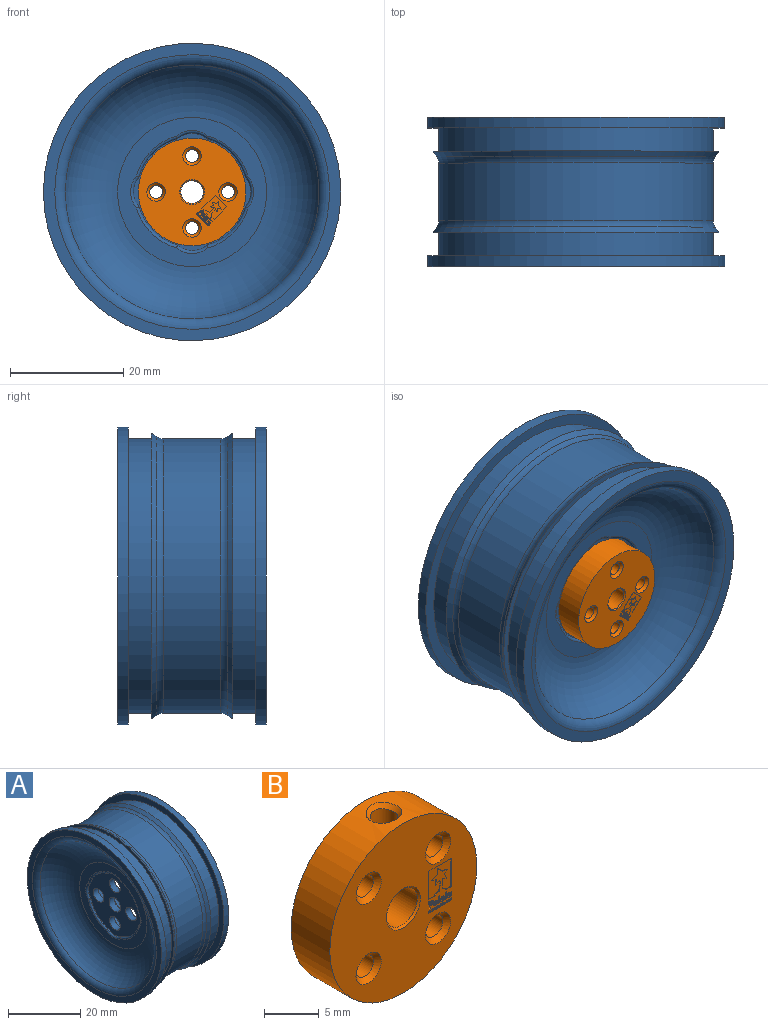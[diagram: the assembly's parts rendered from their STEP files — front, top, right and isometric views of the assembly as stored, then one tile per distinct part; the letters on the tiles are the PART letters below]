
ASSEMBLY  parts=2 mates=1
PART A: 63 faces, bbox 30.2x55.6x55.6 mm
  f0: cylinder r=9.75mm len=6.81mm, axis (-1,0,0), area 1mm2, adj f33,f45,f46,f54
  f1: cylinder r=9.75mm len=6.81mm, axis (-1,0,0), area 1mm2, adj f33,f43,f46,f50
  f2: cylinder r=9.75mm len=6.81mm, axis (-1,0,0), area 1mm2, adj f33,f44,f45,f51
  f3: cylinder r=9.75mm len=6.81mm, axis (-1,0,0), area 1mm2, adj f33,f43,f44,f47
  f4: cylinder r=9.75mm len=6.81mm, axis (1,0,0), area 1mm2, adj f34,f41,f42,f58
  f5: cylinder r=9.75mm len=6.81mm, axis (1,0,0), area 1mm2, adj f34,f40,f42,f62
  f6: cylinder r=9.75mm len=6.81mm, axis (1,0,0), area 1mm2, adj f34,f39,f41,f55
  f7: cylinder r=9.75mm len=6.81mm, axis (1,0,0), area 1mm2, adj f34,f39,f40,f59
  f8: cylinder r=2.25mm len=4.5mm, axis (-1,0,0), area 28.3mm2, adj f33,f34
  f9: plane 52.5x52.5mm, normal (1,0,0), area 317.3mm2, adj f10,f30
  f10: cylinder r=26.25mm len=52.5mm, axis (1,0,0), area 305.1mm2, adj f9,f11
  f11: plane 52.5x52.5mm, normal (-1,0,0), area 317.3mm2, adj f10,f12
  f12: torus R=24.25mm, axis (1,0,0), area 343.3mm2, adj f11,f13
  f13: torus R=13.17mm, axis (1,0,0), area 1361.5mm2, adj f12,f14
  f14: plane 26.33x26.33mm, normal (-1,0,0), area 205.2mm2, adj f13,f47,f48,f49,f50,f51,f52,f53
  f15: cylinder r=12.95mm len=25.89mm, axis (1,0,0), area 3.3mm2, adj f16,f31
  f16: torus R=12.25mm, axis (1,0,0), area 1782.1mm2, adj f15,f17
  f17: cylinder r=22.25mm len=44.5mm, axis (1,0,0), area 529.5mm2, adj f16,f18
  f18: torus R=24.25mm, axis (1,0,0), area 453.5mm2, adj f17,f19
  f19: plane 52.5x52.5mm, normal (1,0,0), area 317.3mm2, adj f18,f20
  f20: cylinder r=26.25mm len=52.5mm, axis (1,0,0), area 305.1mm2, adj f19,f21
  f21: plane 52.5x52.5mm, normal (-1,0,0), area 317.3mm2, adj f20,f22
  f22: cylinder r=24.25mm len=48.5mm, axis (1,0,0), area 624.7mm2, adj f21,f23
  f23: plane 50.5x50.5mm, normal (1,0,0), area 155.5mm2, adj f22,f24
  f24: cone r=25.25mm half-angle=33.7deg, axis (1,0,0), area 187.4mm2, adj f23,f25
  f25: torus R=26.25mm, axis (1,0,0), area 180mm2, adj f24,f26
  f26: cylinder r=24.25mm len=48.5mm, axis (1,0,0), area 1552.5mm2, adj f25,f27
  f27: torus R=26.25mm, axis (1,0,0), area 180mm2, adj f26,f28
  f28: cone r=24.59mm half-angle=33.7deg, axis (-1,0,0), area 187.4mm2, adj f27,f29
  f29: plane 50.5x50.5mm, normal (-1,0,0), area 155.5mm2, adj f28,f30
  f30: cylinder r=24.25mm len=48.5mm, axis (1,0,0), area 624.7mm2, adj f9,f29
  f31: cylinder r=12.95mm len=25.89mm, axis (-1,0,0), area 1.9mm2, adj f15,f32
  f32: plane 25.89x25.89mm, normal (1,0,0), area 187mm2, adj f31,f55,f56,f57,f58,f59,f60,f61
  f33: plane 20.7x20.7mm, normal (-1,0,0), area 235.9mm2, adj f0,f1,f2,f3,f8,f35,f36,f37
  f34: plane 20.7x20.7mm, normal (1,0,0), area 235.9mm2, adj f4,f5,f6,f7,f8,f35,f36,f37
  f35: cylinder r=2.1mm len=4.2mm, axis (1,0,0), area 26.4mm2, adj f33,f34
  f36: cylinder r=2.1mm len=4.2mm, axis (1,0,0), area 26.4mm2, adj f33,f34
  f37: cylinder r=2.1mm len=4.2mm, axis (1,0,0), area 26.4mm2, adj f33,f34
  f38: cylinder r=2.1mm len=4.2mm, axis (1,0,0), area 26.4mm2, adj f33,f34
  f39: cylinder r=4mm len=5.18mm, axis (-1,0,0), area 0.6mm2, adj f6,f7,f34,f57
  f40: cylinder r=4mm len=5.18mm, axis (-1,0,0), area 0.6mm2, adj f5,f7,f34,f61
  f41: cylinder r=4mm len=5.18mm, axis (-1,0,0), area 0.6mm2, adj f4,f6,f34,f56
  f42: cylinder r=4mm len=5.18mm, axis (-1,0,0), area 0.6mm2, adj f4,f5,f34,f60
  f43: cylinder r=4mm len=5.18mm, axis (1,0,0), area 0.6mm2, adj f1,f3,f33,f48
  f44: cylinder r=4mm len=5.18mm, axis (1,0,0), area 0.6mm2, adj f2,f3,f33,f49
  f45: cylinder r=4mm len=5.18mm, axis (1,0,0), area 0.6mm2, adj f0,f2,f33,f53
  f46: cylinder r=4mm len=5.18mm, axis (1,0,0), area 0.6mm2, adj f0,f1,f33,f52
  f47: torus R=10.25mm, axis (-1,0,0), area 8mm2, adj f3,f14,f48,f49
  f48: torus R=4.5mm, axis (-1,0,0), area 4.5mm2, adj f14,f43,f47,f50
  f49: torus R=4.5mm, axis (-1,0,0), area 4.5mm2, adj f14,f44,f47,f51
  f50: torus R=10.25mm, axis (-1,0,0), area 8mm2, adj f1,f14,f48,f52
  f51: torus R=10.25mm, axis (-1,0,0), area 8mm2, adj f2,f14,f49,f53
  f52: torus R=4.5mm, axis (-1,0,0), area 4.5mm2, adj f14,f46,f50,f54
  f53: torus R=4.5mm, axis (-1,0,0), area 4.5mm2, adj f14,f45,f51,f54
  f54: torus R=10.25mm, axis (-1,0,0), area 8mm2, adj f0,f14,f52,f53
  f55: torus R=10.25mm, axis (-1,0,0), area 8mm2, adj f6,f32,f56,f57
  f56: torus R=4.5mm, axis (-1,0,0), area 4.5mm2, adj f32,f41,f55,f58
  f57: torus R=4.5mm, axis (-1,0,0), area 4.5mm2, adj f32,f39,f55,f59
  f58: torus R=10.25mm, axis (-1,0,0), area 8mm2, adj f4,f32,f56,f60
  f59: torus R=10.25mm, axis (-1,0,0), area 8mm2, adj f7,f32,f57,f61
  f60: torus R=4.5mm, axis (-1,0,0), area 4.5mm2, adj f32,f42,f58,f62
  f61: torus R=4.5mm, axis (-1,0,0), area 4.5mm2, adj f32,f40,f59,f62
  f62: torus R=10.25mm, axis (-1,0,0), area 8mm2, adj f5,f32,f60,f61
PART B: 267 faces, bbox 19x5x19 mm
  f0: bspline ~3.36x3.21mm, area 5.4mm2, adj f11,f17
  f1: cone r=2mm half-angle=45deg, axis (0,-1,0), area 3.7mm2, adj f12,f18
  f2: cone r=2mm half-angle=45deg, axis (0,1,0), area 3.7mm2, adj f12,f19
  f3: cone r=1.13mm half-angle=45deg, axis (0,1,0), area 6.1mm2, adj f14,f19
  f4: cone r=1.13mm half-angle=45deg, axis (0,1,0), area 6.1mm2, adj f15,f19
  f5: cone r=1.13mm half-angle=45deg, axis (0,1,0), area 6.1mm2, adj f16,f19
  f6: cone r=1.13mm half-angle=45deg, axis (0,1,0), area 6.1mm2, adj f13,f19
  f7: cone r=1.63mm half-angle=45deg, axis (0,-1,0), area 6.1mm2, adj f13,f18
  f8: cone r=1.63mm half-angle=45deg, axis (0,-1,0), area 6.1mm2, adj f14,f18
  f9: cone r=1.63mm half-angle=45deg, axis (0,-1,0), area 6.1mm2, adj f16,f18
  f10: cone r=1.63mm half-angle=45deg, axis (0,-1,0), area 6.1mm2, adj f15,f18
  f11: cylinder r=1.25mm len=7.5mm, axis (0,0,1), area 56.6mm2, adj f0,f12
  f12: cylinder r=2mm len=4.6mm, axis (0,1,0), area 54.4mm2, adj f1,f2,f11
  f13: cylinder r=1.13mm len=4mm, axis (0,1,0), area 28.4mm2, adj f6,f7
  f14: cylinder r=1.13mm len=4mm, axis (0,1,0), area 28.4mm2, adj f3,f8
  f15: cylinder r=1.13mm len=4mm, axis (0,1,0), area 28.4mm2, adj f4,f10
  f16: cylinder r=1.13mm len=4mm, axis (0,1,0), area 28.4mm2, adj f5,f9
  f17: cylinder r=9.5mm len=19mm, axis (0,-1,0), area 289.9mm2, adj f0,f18,f19
  f18: plane 19x19mm, normal (0,-1,0), area 226.4mm2, adj f1,f7,f8,f9,f10,f17,f20,f21
  f19: plane 19x19mm, normal (0,1,0), area 234.9mm2, adj f2,f3,f4,f5,f6,f17
  f20: plane 0.05x0.04mm, normal (0,0,-1), area 0mm2, adj f18,f21,f32,f33
  f21: plane 0.2x0.05mm, normal (-0.97,0,0.25), area 0mm2, adj f18,f20,f22,f33
  f22: plane 0.05x0.03mm, normal (0,0,1), area 0mm2, adj f18,f21,f23,f33
  f23: plane 0.16x0.05mm, normal (0.95,0,0.31), area 0mm2, adj f18,f22,f24,f33
  f24: plane 0.16x0.05mm, normal (-0.95,0,0.31), area 0mm2, adj f18,f23,f25,f33
  f25: plane 0.05x0.03mm, normal (0,0,1), area 0mm2, adj f18,f24,f26,f33
  f26: plane 0.2x0.05mm, normal (0.97,0,0.25), area 0mm2, adj f18,f25,f27,f33
  f27: plane 0.05x0.04mm, normal (0,0,-1), area 0mm2, adj f18,f26,f28,f33
  f28: plane 0.16x0.05mm, normal (-0.97,0,-0.23), area 0mm2, adj f18,f27,f29,f33
  f29: plane 0.16x0.05mm, normal (0.95,0,-0.31), area 0mm2, adj f18,f28,f30,f33
  f30: plane 0.05x0.03mm, normal (0,0,-1), area 0mm2, adj f18,f29,f31,f33
  f31: plane 0.16x0.05mm, normal (-0.95,0,-0.31), area 0mm2, adj f18,f30,f32,f33
  f32: plane 0.16x0.05mm, normal (0.98,0,-0.21), area 0mm2, adj f18,f20,f31,f33
  f33: plane 0.27x0.2mm, normal (0,-1,0), area 0mm2, adj f20,f21,f22,f23,f24,f25,f26,f27
  f34: plane 0.05x0.04mm, normal (0,0,-1), area 0mm2, adj f18,f35,f46,f47
  f35: plane 0.2x0.05mm, normal (-0.97,0,0.25), area 0mm2, adj f18,f34,f36,f47
  f36: plane 0.05x0.03mm, normal (0,0,1), area 0mm2, adj f18,f35,f37,f47
  f37: plane 0.16x0.05mm, normal (0.95,0,0.31), area 0mm2, adj f18,f36,f38,f47
  f38: plane 0.16x0.05mm, normal (-0.95,0,0.31), area 0mm2, adj f18,f37,f39,f47
  f39: plane 0.05x0.03mm, normal (0,0,1), area 0mm2, adj f18,f38,f40,f47
  f40: plane 0.2x0.05mm, normal (0.97,0,0.25), area 0mm2, adj f18,f39,f41,f47
  f41: plane 0.05x0.04mm, normal (0,0,-1), area 0mm2, adj f18,f40,f42,f47
  f42: plane 0.16x0.05mm, normal (-0.97,0,-0.23), area 0mm2, adj f18,f41,f43,f47
  f43: plane 0.16x0.05mm, normal (0.95,0,-0.31), area 0mm2, adj f18,f42,f44,f47
  f44: plane 0.05x0.03mm, normal (0,0,-1), area 0mm2, adj f18,f43,f45,f47
  f45: plane 0.16x0.05mm, normal (-0.95,0,-0.31), area 0mm2, adj f18,f44,f46,f47
  f46: plane 0.16x0.05mm, normal (0.98,0,-0.21), area 0mm2, adj f18,f34,f45,f47
  f47: plane 0.27x0.2mm, normal (0,-1,0), area 0mm2, adj f34,f35,f36,f37,f38,f39,f40,f41
  f48: plane 0.05x0.04mm, normal (0,0,-1), area 0mm2, adj f18,f49,f60,f61
  f49: plane 0.2x0.05mm, normal (-0.97,0,0.25), area 0mm2, adj f18,f48,f50,f61
  f50: plane 0.05x0.03mm, normal (0,0,1), area 0mm2, adj f18,f49,f51,f61
  f51: plane 0.16x0.05mm, normal (0.95,0,0.31), area 0mm2, adj f18,f50,f52,f61
  f52: plane 0.16x0.05mm, normal (-0.95,0,0.31), area 0mm2, adj f18,f51,f53,f61
  f53: plane 0.05x0.03mm, normal (0,0,1), area 0mm2, adj f18,f52,f54,f61
  f54: plane 0.2x0.05mm, normal (0.97,0,0.25), area 0mm2, adj f18,f53,f55,f61
  f55: plane 0.05x0.04mm, normal (0,0,-1), area 0mm2, adj f18,f54,f56,f61
  f56: plane 0.16x0.05mm, normal (-0.97,0,-0.23), area 0mm2, adj f18,f55,f57,f61
  f57: plane 0.16x0.05mm, normal (0.95,0,-0.31), area 0mm2, adj f18,f56,f58,f61
  f58: plane 0.05x0.03mm, normal (0,0,-1), area 0mm2, adj f18,f57,f59,f61
  f59: plane 0.16x0.05mm, normal (-0.95,0,-0.31), area 0mm2, adj f18,f58,f60,f61
  f60: plane 0.16x0.05mm, normal (0.98,0,-0.21), area 0mm2, adj f18,f48,f59,f61
  f61: plane 0.27x0.2mm, normal (0,-1,0), area 0mm2, adj f48,f49,f50,f51,f52,f53,f54,f55
  f62: plane 0.05x0.05mm, normal (-1,0,0), area 0mm2, adj f18,f63,f65,f66
  f63: plane 0.05x0.04mm, normal (0,0,1), area 0mm2, adj f18,f62,f64,f66
  f64: plane 0.05x0.05mm, normal (1,0,0), area 0mm2, adj f18,f63,f65,f66
  f65: plane 0.05x0.04mm, normal (0,0,-1), area 0mm2, adj f18,f62,f64,f66
  f66: plane 0.05x0.04mm, normal (0,-1,0), area 0mm2, adj f62,f63,f64,f65
  f67: bspline ~0.1x0.08mm, area 0mm2, adj f18,f68,f76,f77
  f68: bspline ~0.08x0.05mm, area 0mm2, adj f18,f67,f69,f77
  f69: bspline ~0.06x0.05mm, area 0mm2, adj f18,f68,f70,f77
  f70: bspline ~0.05x0.05mm, area 0mm2, adj f18,f69,f71,f77
  f71: plane 0.09x0.05mm, normal (-1,0,0), area 0mm2, adj f18,f70,f72,f77
  f72: plane 0.05x0.03mm, normal (0,0,1), area 0mm2, adj f18,f71,f73,f77
  f73: plane 0.28x0.05mm, normal (1,0,0), area 0mm2, adj f18,f72,f74,f77
  f74: plane 0.05x0.03mm, normal (0,0,-1), area 0mm2, adj f18,f73,f75,f77
  f75: plane 0.05x0.02mm, normal (-1,0,0), area 0mm2, adj f18,f74,f76,f77
  f76: bspline ~0.07x0.05mm, area 0mm2, adj f18,f67,f75,f77
  f77: plane 0.28x0.17mm, normal (0,-1,0), area 0mm2, adj f67,f68,f69,f70,f71,f72,f73,f74
  f78: bspline ~0.08x0.06mm, area 0mm2, adj f77,f79,f82,f83
  f79: bspline ~0.05x0.05mm, area 0mm2, adj f77,f78,f80,f83
  f80: plane 0.12x0.05mm, normal (-1,0,0), area 0mm2, adj f77,f79,f81,f83
  f81: bspline ~0.06x0.05mm, area 0mm2, adj f77,f80,f82,f83
  f82: bspline ~0.07x0.05mm, area 0mm2, adj f77,f78,f81,f83
  f83: plane 0.15x0.11mm, normal (0,-1,0), area 0mm2, adj f78,f79,f80,f81,f82
  f84: bspline ~0.11x0.09mm, area 0mm2, adj f18,f85,f87,f88
  f85: bspline ~0.11x0.09mm, area 0mm2, adj f18,f84,f86,f88
  f86: bspline ~0.11x0.09mm, area 0mm2, adj f18,f85,f87,f88
  f87: bspline ~0.11x0.09mm, area 0mm2, adj f18,f84,f86,f88
  f88: plane 0.22x0.18mm, normal (0,-1,0), area 0mm2, adj f84,f85,f86,f87,f89,f90,f91,f92
  f89: bspline ~0.08x0.06mm, area 0mm2, adj f88,f90,f92,f93
  f90: bspline ~0.08x0.06mm, area 0mm2, adj f88,f89,f91,f93
  f91: bspline ~0.08x0.06mm, area 0mm2, adj f88,f90,f92,f93
  f92: bspline ~0.08x0.06mm, area 0mm2, adj f88,f89,f91,f93
  f93: plane 0.15x0.12mm, normal (0,-1,0), area 0mm2, adj f89,f90,f91,f92
  f94: plane 0.28x0.05mm, normal (-1,0,0), area 0mm2, adj f18,f95,f97,f98
  f95: plane 0.05x0.03mm, normal (0,0,1), area 0mm2, adj f18,f94,f96,f98
  f96: plane 0.28x0.05mm, normal (1,0,0), area 0mm2, adj f18,f95,f97,f98
  f97: plane 0.05x0.03mm, normal (0,0,-1), area 0mm2, adj f18,f94,f96,f98
  f98: plane 0.28x0.03mm, normal (0,-1,0), area 0mm2, adj f94,f95,f96,f97
  f99: bspline ~0.11x0.09mm, area 0mm2, adj f18,f100,f102,f103
  f100: bspline ~0.11x0.09mm, area 0mm2, adj f18,f99,f101,f103
  f101: bspline ~0.11x0.09mm, area 0mm2, adj f18,f100,f102,f103
  f102: bspline ~0.11x0.09mm, area 0mm2, adj f18,f99,f101,f103
  f103: plane 0.22x0.18mm, normal (0,-1,0), area 0mm2, adj f99,f100,f101,f102,f104,f105,f106,f107
  f104: bspline ~0.08x0.06mm, area 0mm2, adj f103,f105,f107,f108
  f105: bspline ~0.08x0.06mm, area 0mm2, adj f103,f104,f106,f108
  f106: bspline ~0.08x0.06mm, area 0mm2, adj f103,f105,f107,f108
  f107: bspline ~0.08x0.06mm, area 0mm2, adj f103,f104,f106,f108
  f108: plane 0.15x0.12mm, normal (0,-1,0), area 0mm2, adj f104,f105,f106,f107
  f109: plane 0.28x0.05mm, normal (-1,0,0), area 0mm2, adj f18,f110,f112,f113
  f110: plane 0.05x0.03mm, normal (0,0,1), area 0mm2, adj f18,f109,f111,f113
  f111: plane 0.28x0.05mm, normal (1,0,0), area 0mm2, adj f18,f110,f112,f113
  f112: plane 0.05x0.03mm, normal (0,0,-1), area 0mm2, adj f18,f109,f111,f113
  f113: plane 0.28x0.03mm, normal (0,-1,0), area 0mm2, adj f109,f110,f111,f112
  f114: plane 0.2x0.05mm, normal (-1,0,0), area 0mm2, adj f18,f115,f126,f127
  f115: plane 0.05x0.03mm, normal (0,0,1), area 0mm2, adj f18,f114,f116,f127
  f116: plane 0.05x0.02mm, normal (1,0,0), area 0mm2, adj f18,f115,f117,f127
  f117: bspline ~0.07x0.05mm, area 0mm2, adj f18,f116,f118,f127
  f118: bspline ~0.08x0.07mm, area 0mm2, adj f18,f117,f119,f127
  f119: plane 0.13x0.05mm, normal (1,0,0), area 0mm2, adj f18,f118,f120,f127
  f120: plane 0.05x0.03mm, normal (0,0,-1), area 0mm2, adj f18,f119,f121,f127
  f121: plane 0.12x0.05mm, normal (-1,0,0), area 0mm2, adj f18,f120,f122,f127
  f122: bspline ~0.05x0.05mm, area 0mm2, adj f18,f121,f123,f127
  f123: bspline ~0.05x0.03mm, area 0mm2, adj f18,f122,f124,f127
  f124: bspline ~0.06x0.05mm, area 0mm2, adj f18,f123,f125,f127
  f125: plane 0.15x0.05mm, normal (1,0,0), area 0mm2, adj f18,f124,f126,f127
  f126: plane 0.05x0.03mm, normal (0,0,-1), area 0mm2, adj f18,f114,f125,f127
  f127: plane 0.21x0.17mm, normal (0,-1,0), area 0mm2, adj f114,f115,f116,f117,f118,f119,f120,f121
  f128: plane 0.05x0.05mm, normal (-1,0,0), area 0mm2, adj f18,f129,f131,f132
  f129: plane 0.05x0.04mm, normal (0,0,1), area 0mm2, adj f18,f128,f130,f132
  f130: plane 0.05x0.05mm, normal (1,0,0), area 0mm2, adj f18,f129,f131,f132
  f131: plane 0.05x0.04mm, normal (0,0,-1), area 0mm2, adj f18,f128,f130,f132
  f132: plane 0.05x0.04mm, normal (0,-1,0), area 0mm2, adj f128,f129,f130,f131
  f133: plane 0.05x0.04mm, normal (-1,0,0), area 0mm2, adj f18,f134,f146,f147
  f134: bspline ~0.06x0.05mm, area 0mm2, adj f18,f133,f135,f147
  f135: bspline ~0.07x0.05mm, area 0mm2, adj f18,f134,f136,f147
  f136: bspline ~0.08x0.05mm, area 0mm2, adj f18,f135,f137,f147
  f137: bspline ~0.11x0.1mm, area 0mm2, adj f18,f136,f138,f147
  f138: bspline ~0.06x0.05mm, area 0mm2, adj f18,f137,f139,f147
  f139: plane 0.05x0.04mm, normal (-1,0,0), area 0mm2, adj f18,f138,f140,f147
  f140: plane 0.05x0mm, normal (0,0,1), area 0mm2, adj f18,f139,f141,f147
  f141: bspline ~0.06x0.05mm, area 0mm2, adj f18,f140,f142,f147
  f142: bspline ~0.08x0.06mm, area 0mm2, adj f18,f141,f143,f147
  f143: bspline ~0.07x0.06mm, area 0mm2, adj f18,f142,f144,f147
  f144: bspline ~0.05x0.04mm, area 0mm2, adj f18,f143,f145,f147
  f145: bspline ~0.05x0.02mm, area 0mm2, adj f18,f144,f146,f147
  f146: plane 0.05x0mm, normal (0,0,-1), area 0mm2, adj f18,f133,f145,f147
  f147: plane 0.21x0.16mm, normal (0,-1,0), area 0mm2, adj f133,f134,f135,f136,f137,f138,f139,f140
  f148: bspline ~0.11x0.09mm, area 0mm2, adj f18,f149,f151,f152
  f149: bspline ~0.11x0.09mm, area 0mm2, adj f18,f148,f150,f152
  f150: bspline ~0.11x0.09mm, area 0mm2, adj f18,f149,f151,f152
  f151: bspline ~0.11x0.09mm, area 0mm2, adj f18,f148,f150,f152
  f152: plane 0.22x0.18mm, normal (0,-1,0), area 0mm2, adj f148,f149,f150,f151,f153,f154,f155,f156
  f153: bspline ~0.08x0.06mm, area 0mm2, adj f152,f154,f156,f157
  f154: bspline ~0.08x0.06mm, area 0mm2, adj f152,f153,f155,f157
  f155: bspline ~0.08x0.06mm, area 0mm2, adj f152,f154,f156,f157
  f156: bspline ~0.08x0.06mm, area 0mm2, adj f152,f153,f155,f157
  f157: plane 0.15x0.12mm, normal (0,-1,0), area 0mm2, adj f153,f154,f155,f156
  f158: plane 0.13x0.05mm, normal (-1,0,0), area 0mm2, adj f18,f159,f179,f180
  f159: plane 0.05x0.03mm, normal (0,0,1), area 0mm2, adj f18,f158,f160,f180
  f160: plane 0.12x0.05mm, normal (1,0,0), area 0mm2, adj f18,f159,f161,f180
  f161: bspline ~0.05x0.05mm, area 0mm2, adj f18,f160,f162,f180
  f162: bspline ~0.05x0.03mm, area 0mm2, adj f18,f161,f163,f180
  f163: bspline ~0.06x0.05mm, area 0mm2, adj f18,f162,f164,f180
  f164: bspline ~0.05x0.02mm, area 0mm2, adj f18,f163,f165,f180
  f165: plane 0.13x0.05mm, normal (-1,0,0), area 0mm2, adj f18,f164,f166,f180
  f166: plane 0.05x0.03mm, normal (0,0,1), area 0mm2, adj f18,f165,f167,f180
  f167: plane 0.12x0.05mm, normal (1,0,0), area 0mm2, adj f18,f166,f168,f180
  f168: bspline ~0.05x0.05mm, area 0mm2, adj f18,f167,f169,f180
  f169: bspline ~0.05x0.03mm, area 0mm2, adj f18,f168,f170,f180
  f170: bspline ~0.06x0.05mm, area 0mm2, adj f18,f169,f171,f180
  f171: plane 0.15x0.05mm, normal (-1,0,0), area 0mm2, adj f18,f170,f172,f180
  f172: plane 0.05x0.03mm, normal (0,0,1), area 0mm2, adj f18,f171,f173,f180
  f173: plane 0.2x0.05mm, normal (1,0,0), area 0mm2, adj f18,f172,f174,f180
  f174: plane 0.05x0.03mm, normal (0,0,-1), area 0mm2, adj f18,f173,f175,f180
  f175: plane 0.05x0.02mm, normal (-1,0,0), area 0mm2, adj f18,f174,f176,f180
  f176: bspline ~0.07x0.05mm, area 0mm2, adj f18,f175,f177,f180
  f177: bspline ~0.06x0.05mm, area 0mm2, adj f18,f176,f178,f180
  f178: bspline ~0.07x0.05mm, area 0mm2, adj f18,f177,f179,f180
  f179: bspline ~0.08x0.06mm, area 0mm2, adj f18,f158,f178,f180
  f180: plane 0.29x0.21mm, normal (0,-1,0), area 0mm2, adj f158,f159,f160,f161,f162,f163,f164,f165
  f181: bspline ~0.24x0.24mm, area 0mm2, adj f18,f182,f190,f191
  f182: plane 0.29x0.05mm, normal (1,0,0), area 0mm2, adj f18,f181,f183,f191
  f183: plane 0.17x0.05mm, normal (0,0,-1), area 0mm2, adj f18,f182,f184,f191
  f184: plane 0.3x0.05mm, normal (-1,0,0), area 0mm2, adj f18,f183,f185,f191
  f185: bspline ~0.09x0.08mm, area 0mm2, adj f18,f184,f186,f191
  f186: bspline ~0.08x0.08mm, area 0mm2, adj f18,f185,f187,f191
  f187: plane 0.3x0.05mm, normal (1,0,0), area 0mm2, adj f18,f186,f188,f191
  f188: plane 0.17x0.05mm, normal (0,0,-1), area 0mm2, adj f18,f187,f189,f191
  f189: plane 0.29x0.05mm, normal (-1,0,0), area 0mm2, adj f18,f188,f190,f191
  f190: bspline ~0.25x0.24mm, area 0mm2, adj f18,f181,f189,f191
  f191: plane 0.53x0.49mm, normal (0,-1,0), area 0.2mm2, adj f181,f182,f183,f184,f185,f186,f187,f188
  f192: bspline ~0.28x0.26mm, area 0mm2, adj f18,f193,f197,f198
  f193: plane 0.05x0mm, normal (1,0,0), area 0mm2, adj f18,f192,f194,f198
  f194: bspline ~0.28x0.27mm, area 0mm2, adj f18,f193,f195,f198
  f195: bspline ~0.28x0.26mm, area 0mm2, adj f18,f194,f196,f198
  f196: plane 0.05x0mm, normal (-1,0,0), area 0mm2, adj f18,f195,f197,f198
  f197: bspline ~0.28x0.27mm, area 0mm2, adj f18,f192,f196,f198
  f198: plane 0.55x0.53mm, normal (0,-1,0), area 0.2mm2, adj f192,f193,f194,f195,f196,f197,f199,f200
  f199: bspline ~0.12x0.12mm, area 0mm2, adj f198,f200,f204,f205
  f200: bspline ~0.13x0.12mm, area 0mm2, adj f198,f199,f201,f205
  f201: plane 0.05x0mm, normal (-1,0,0), area 0mm2, adj f198,f200,f202,f205
  f202: bspline ~0.12x0.12mm, area 0mm2, adj f198,f201,f203,f205
  f203: bspline ~0.13x0.12mm, area 0mm2, adj f198,f202,f204,f205
  f204: plane 0.05x0mm, normal (1,0,0), area 0mm2, adj f198,f199,f203,f205
  f205: plane 0.25x0.24mm, normal (0,-1,0), area 0mm2, adj f199,f200,f201,f202,f203,f204
  f206: plane 0.81x0.05mm, normal (1,0,0), area 0mm2, adj f18,f207,f209,f210
  f207: plane 0.17x0.05mm, normal (0,0,-1), area 0mm2, adj f18,f206,f208,f210
  f208: plane 0.81x0.05mm, normal (-1,0,0), area 0mm2, adj f18,f207,f209,f210
  f209: plane 0.17x0.05mm, normal (0,0,1), area 0mm2, adj f18,f206,f208,f210
  f210: plane 0.81x0.17mm, normal (0,-1,0), area 0.1mm2, adj f206,f207,f208,f209
  f211: bspline ~0.28x0.26mm, area 0mm2, adj f18,f212,f216,f217
  f212: plane 0.05x0mm, normal (1,0,0), area 0mm2, adj f18,f211,f213,f217
  f213: bspline ~0.28x0.27mm, area 0mm2, adj f18,f212,f214,f217
  f214: bspline ~0.28x0.26mm, area 0mm2, adj f18,f213,f215,f217
  f215: plane 0.05x0mm, normal (-1,0,0), area 0mm2, adj f18,f214,f216,f217
  f216: bspline ~0.28x0.27mm, area 0mm2, adj f18,f211,f215,f217
  f217: plane 0.55x0.53mm, normal (0,-1,0), area 0.2mm2, adj f211,f212,f213,f214,f215,f216,f218,f219
  f218: bspline ~0.12x0.12mm, area 0mm2, adj f217,f219,f223,f224
  f219: bspline ~0.13x0.12mm, area 0mm2, adj f217,f218,f220,f224
  f220: plane 0.05x0mm, normal (-1,0,0), area 0mm2, adj f217,f219,f221,f224
  f221: bspline ~0.12x0.12mm, area 0mm2, adj f217,f220,f222,f224
  f222: bspline ~0.13x0.12mm, area 0mm2, adj f217,f221,f223,f224
  f223: plane 0.05x0mm, normal (1,0,0), area 0mm2, adj f217,f218,f222,f224
  f224: plane 0.25x0.24mm, normal (0,-1,0), area 0mm2, adj f218,f219,f220,f221,f222,f223
  f225: plane 0.81x0.05mm, normal (1,0,0), area 0mm2, adj f18,f226,f228,f229
  f226: plane 0.17x0.05mm, normal (0,0,-1), area 0mm2, adj f18,f225,f227,f229
  f227: plane 0.81x0.05mm, normal (-1,0,0), area 0mm2, adj f18,f226,f228,f229
  f228: plane 0.17x0.05mm, normal (0,0,1), area 0mm2, adj f18,f225,f227,f229
  f229: plane 0.81x0.17mm, normal (0,-1,0), area 0.1mm2, adj f225,f226,f227,f228
  f230: bspline ~0.3x0.27mm, area 0mm2, adj f18,f231,f237,f238
  f231: plane 0.05x0mm, normal (-1,0,0), area 0mm2, adj f18,f230,f232,f238
  f232: bspline ~0.31x0.27mm, area 0mm2, adj f18,f231,f233,f238
  f233: plane 0.08x0.05mm, normal (0,0,1), area 0mm2, adj f18,f232,f234,f238
  f234: plane 0.27x0.05mm, normal (-1,0,0), area 0mm2, adj f18,f233,f235,f238
  f235: plane 0.17x0.05mm, normal (0,0,1), area 0mm2, adj f18,f234,f236,f238
  f236: plane 0.81x0.05mm, normal (1,0,0), area 0mm2, adj f18,f235,f237,f238
  f237: plane 0.27x0.05mm, normal (0,0,-1), area 0mm2, adj f18,f230,f236,f238
  f238: plane 0.81x0.57mm, normal (0,-1,0), area 0.3mm2, adj f230,f231,f232,f233,f234,f235,f236,f237
  f239: bspline ~0.14x0.12mm, area 0mm2, adj f238,f240,f244,f245
  f240: plane 0.09x0.05mm, normal (0,0,-1), area 0mm2, adj f238,f239,f241,f245
  f241: plane 0.24x0.05mm, normal (-1,0,0), area 0mm2, adj f238,f240,f242,f245
  f242: plane 0.08x0.05mm, normal (0,0,1), area 0mm2, adj f238,f241,f243,f245
  f243: bspline ~0.14x0.12mm, area 0mm2, adj f238,f242,f244,f245
  f244: plane 0.05x0mm, normal (1,0,0), area 0mm2, adj f238,f239,f243,f245
  f245: plane 0.24x0.22mm, normal (0,-1,0), area 0mm2, adj f239,f240,f241,f242,f243,f244
  f246: bspline ~0.53x0.29mm, area 0mm2, adj f18,f247,f265,f266
  f247: bspline ~1.17x0.14mm, area 0.1mm2, adj f18,f246,f248,f266
  f248: bspline ~0.56x0.18mm, area 0mm2, adj f18,f247,f249,f266
  f249: bspline ~0.55x0.29mm, area 0mm2, adj f18,f248,f250,f266
  f250: bspline ~0.5x0.32mm, area 0mm2, adj f18,f249,f251,f266
  f251: bspline ~0.73x0.16mm, area 0mm2, adj f18,f250,f252,f266
  f252: bspline ~0.54x0.53mm, area 0mm2, adj f18,f251,f253,f266
  f253: bspline ~0.63x0.08mm, area 0mm2, adj f18,f252,f254,f266
  f254: bspline ~0.66x0.29mm, area 0mm2, adj f18,f253,f255,f266
  f255: bspline ~0.56x0.19mm, area 0mm2, adj f18,f254,f256,f266
  f256: bspline ~0.6x0.15mm, area 0mm2, adj f18,f255,f257,f266
  f257: bspline ~0.56x0.33mm, area 0mm2, adj f18,f256,f258,f266
  f258: bspline ~1.17x0.19mm, area 0.1mm2, adj f18,f257,f259,f266
  f259: bspline ~0.34x0.08mm, area 0mm2, adj f18,f258,f260,f266
  f260: bspline ~0.32x0.19mm, area 0mm2, adj f18,f259,f261,f266
  f261: plane 0.64x0.05mm, normal (0,0,1), area 0mm2, adj f18,f260,f262,f266
  f262: plane 3.18x0.05mm, normal (1,0,0), area 0.2mm2, adj f18,f261,f263,f266
  f263: plane 2.88x0.05mm, normal (0,0,-1), area 0.1mm2, adj f18,f262,f264,f266
  f264: plane 3.18x0.05mm, normal (-1,0,0), area 0.2mm2, adj f18,f263,f265,f266
  f265: plane 0.57x0.05mm, normal (0,0,1), area 0mm2, adj f18,f246,f264,f266
  f266: plane 3.18x2.88mm, normal (0,-1,0), area 7mm2, adj f246,f247,f248,f249,f250,f251,f252,f253
PLACE A rot(axis=(0.58,0.58,0.58),120deg) t=(-5.63,-11.74,-8.66)mm
PLACE B rot(axis=(0,1,0),45deg) t=(-5.63,-6.24,-8.66)mm
MATE revolute B.f1 <-> A.f0  axis (0,1,0) through (-5.63,-3.74,-8.66)mm
